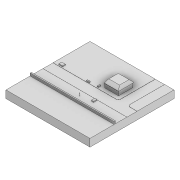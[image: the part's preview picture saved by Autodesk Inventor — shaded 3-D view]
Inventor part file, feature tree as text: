
AUTODESK INVENTOR PART (.ipt)
format: ipt  version: 2021 (Build 250183000, 183)  size: 244,224 bytes
history: native  units: in
note: dims shown in document units (in); Inventor stores cm internally (conversion verified against a paired STEP export)
features: extrude x10, sketch x10, projected_geometry x10, chamfer x2, plane x1, mirror x1, pattern_linear x1
ambient origin geometry x8: Origin, YZ Plane, XZ Plane, XY Plane, X Axis, Y Axis, Z Axis, Center Point
bodies: Solid1 (feature_tree)
feature tree (35):
  extrude  "Extrusion1"  Depth=3937.0079in
  extrude  "Extrusion2"  Depth=472.4409in
  extrude  "Extrusion3"  Depth=118.1102in
  extrude  "Extrusion4"  Depth=196.8504in TaperAngle=0.0deg
  extrude  "Extrusion5"  Depth=23.622in TaperAngle=0.0deg
  plane  "Work Plane1"
  mirror  "Mirror1"
  chamfer  "Chamfer1"  Distance=1.9685in Angle=45.0deg
  chamfer  "Chamfer2"  Distance=137.7953in Angle=45.0deg
  extrude  "Extrusion6"  Depth=118.1102in
  pattern_linear  "Rectangular Pattern1"  Count1=300 Spacing1=0.0in
  extrude  "Extrusion7"  Depth=118.1102in TaperAngle=0.0deg
  extrude  "Extrusion8"  Depth=118.1102in TaperAngle=0.0deg
  extrude  "Extrusion9"  [1 undecoded]
  extrude  "Extrusion10"  [1 undecoded]
  sketch  "Sketch1"  dims[d0=3937.0079in d1=3937.0079in]
  sketch  "Sketch2"  dims[d2=118.1102in d3=0.0in d4=472.4409in]
  projected_geometry  "Projected Loop1"
  sketch  "Sketch3"  dims[d5=433.0709in d6=118.1102in]
  projected_geometry  "Projected Loop2"
  projected_geometry  "Projected Loop3"
  sketch  "Sketch4"  dims[d7=3.937in d8=0.0in d9=196.8504in d10=0.0in]
  projected_geometry  "Projected Loop4"
  sketch  "Sketch5"  dims[d11=196.8504in d12=0.0in d13=23.622in d14=0.0in d15=1.9685in d16=0.125in d17=45.0deg d18=137.7953in d19=0.125in d20=45.0deg]
  projected_geometry  "Projected Loop5"
  sketch  "Sketch6"  dims[d21=19.685in d23=1479.4221in d24=118.1102in d25=0.0in]
  projected_geometry  "Projected Loop6"
  sketch  "Sketch7"  dims[d26=6.2992in d28=196.8504in d29=118.1102in d30=0.0in]
  projected_geometry  "Projected Loop7"
  sketch  "Sketch8"  dims[d31=39.3701in d32=0.0in d33=118.1102in d34=0.0in]
  projected_geometry  "Projected Loop8"
  projected_geometry  "Projected Loop9"
  sketch  "Sketch9"  dims[d35=236.1898in d36=0.0in]
  sketch  "Sketch10"
  projected_geometry  "Projected Loop10"
note: 2 required parameter values undecoded (feature->parameter linkage not recoverable at this tier; creation-order binding heuristic only, values carry confidence <= 0.55)
